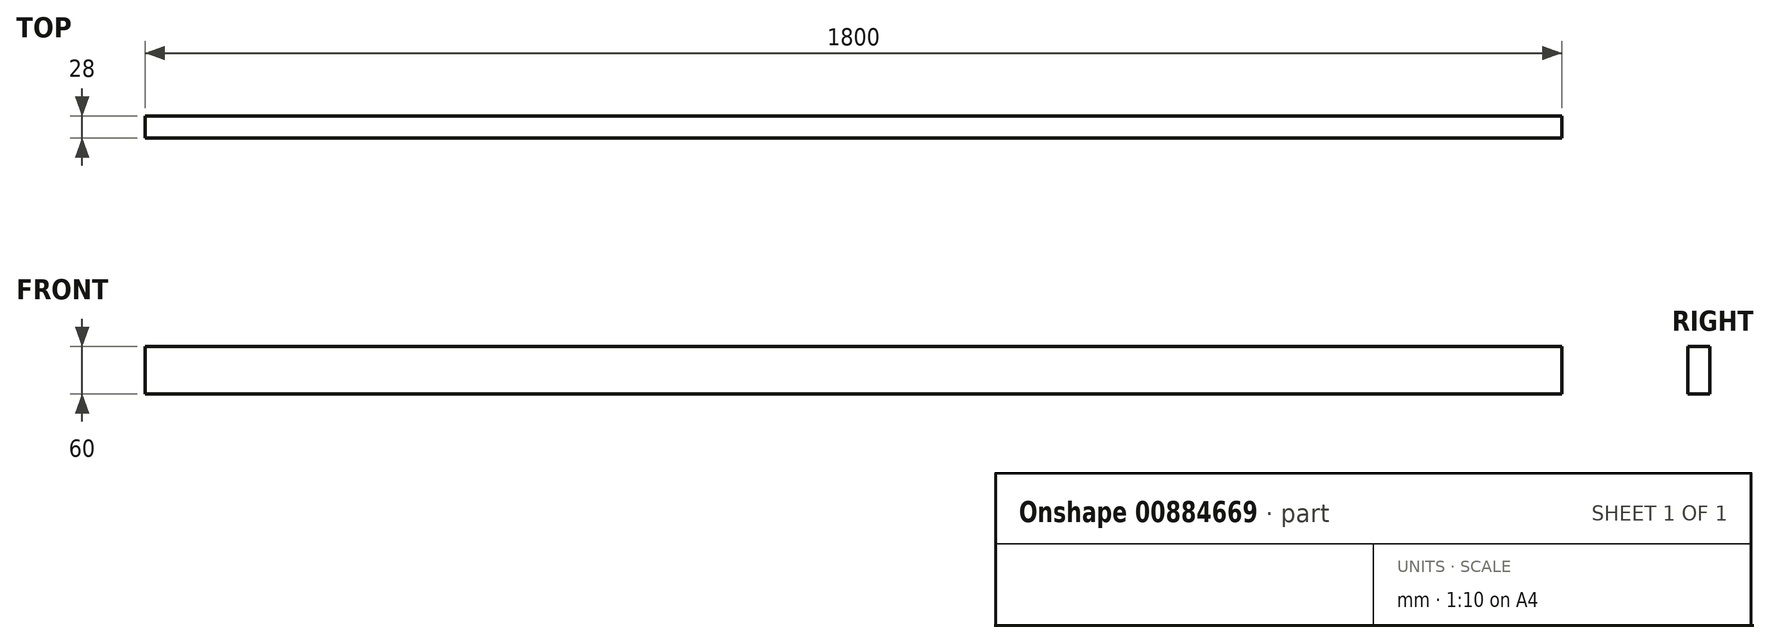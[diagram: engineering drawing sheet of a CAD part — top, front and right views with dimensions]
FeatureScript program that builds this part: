
annotation { "Feature Type Name" : "Feature", "Feature Type Description" : "" }
export const myFeature = defineFeature(function(context is Context, id is Id, definition is map)
    precondition{}
    {
        {
            var Q0;
            Q0=qCreatedBy(makeId("Front.planeOp"),FACE);
            var sketch = newSketch(context, id + "F0", { "sketchPlane" : qUnion([Q0])});
            skLineSegment(sketch, "E0.bottom", {"start": v(900, 30) * mm, "end": v(-900, 30) * mm});
            skLineSegment(sketch, "E0.top", {"start": v(900, -30) * mm, "end": v(-900, -30) * mm});
            skLineSegment(sketch, "E0.left", {"start": v(900, 30) * mm, "end": v(900, -30) * mm});
            skLineSegment(sketch, "E0.right", {"start": v(-900, 30) * mm, "end": v(-900, -30) * mm});
            skPoint(sketch, "E0.middle", {"position": v(0, 0) * mm});
            skSolve(sketch);
        }
        {
            var Q0;
            Q0 = qSketchRegion(id + "F0", true);
            extrude(context, id + "F1", {"entities" : qUnion([Q0]), "depth" : 28 * mm, "offsetDistance" : 25 * mm});
        }
    });
